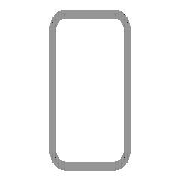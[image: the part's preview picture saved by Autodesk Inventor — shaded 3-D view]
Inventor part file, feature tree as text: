
AUTODESK INVENTOR PART (.ipt)
format: ipt  version: 2025.3 (Build 293356030, 356C)  size: 133,632 bytes
history: native  units: mm (DEFAULTED — no unit token found)
features: other x4, sketch x1, plane x1
ambient origin geometry x8: Origin, YZ Plane, XZ Plane, XY Plane, X Axis, Y Axis, Z Axis, Center Point
bodies: Solid1 (feature_tree), Body (feature_tree)
feature tree (6):
  parser-record x1  (decoder bookkeeping rows leaked as tree rows — omitted from the tree; the rows remain in map.json)
  other  "Driven Length"
  other  "Start Plane"
  other  "End Plane"
  sketch  "Sketch3"  dims[d3=560.0mm d4=0.0mm d7=4.0mm d9=20.0mm d11=40.0mm d12=2.0mm d13=20.0mm d14=580.0mm d15=10.0mm d16=20.0mm d17=90.0deg d18=560.0mm]
  plane  "Work Plane3"
